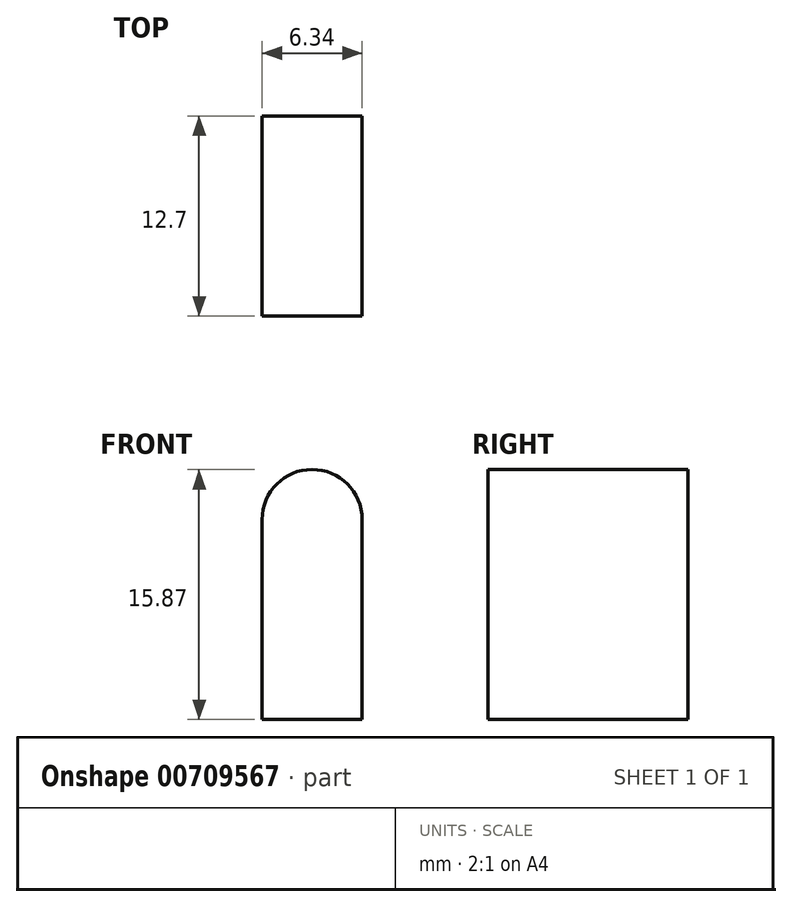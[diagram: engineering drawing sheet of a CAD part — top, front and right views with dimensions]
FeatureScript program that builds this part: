
annotation { "Feature Type Name" : "Feature", "Feature Type Description" : "" }
export const myFeature = defineFeature(function(context is Context, id is Id, definition is map)
    precondition{}
    {
        {
            var Q0;
            Q0=qCreatedBy(makeId("Front.planeOp"),FACE);
            var sketch = newSketch(context, id + "F0", { "sketchPlane" : qUnion([Q0])});
            skLineSegment(sketch, "E0.bottom", {"start": v(3.18, -12.7) * mm, "end": v(-3.17, -12.7) * mm});
            skLineSegment(sketch, "E0.left", {"start": v(-3.17, -12.7) * mm, "end": v(-3.17, 0) * mm});
            skLineSegment(sketch, "E0.right", {"start": v(3.17, -12.7) * mm, "end": v(3.17, 0) * mm});
            skArc(sketch, "E1", {"start": v(-3.17, 0) * mm, "mid": v(0, 3.17) * mm, "end": v(3.17, 0) * mm});
            skSolve(sketch);
        }
        {
            var Q0;
            Q0 = qSketchRegion(id + "F0", true);
            extrude(context, id + "F1", {"entities" : qUnion([Q0]), "depth" : 6.35 * mm, "offsetDistance" : 25.4 * mm, "hasSecondDirection" : true, "secondDirectionOppositeDirection" : true, "secondDirectionDepth" : 6.35 * mm});
        }
    });
